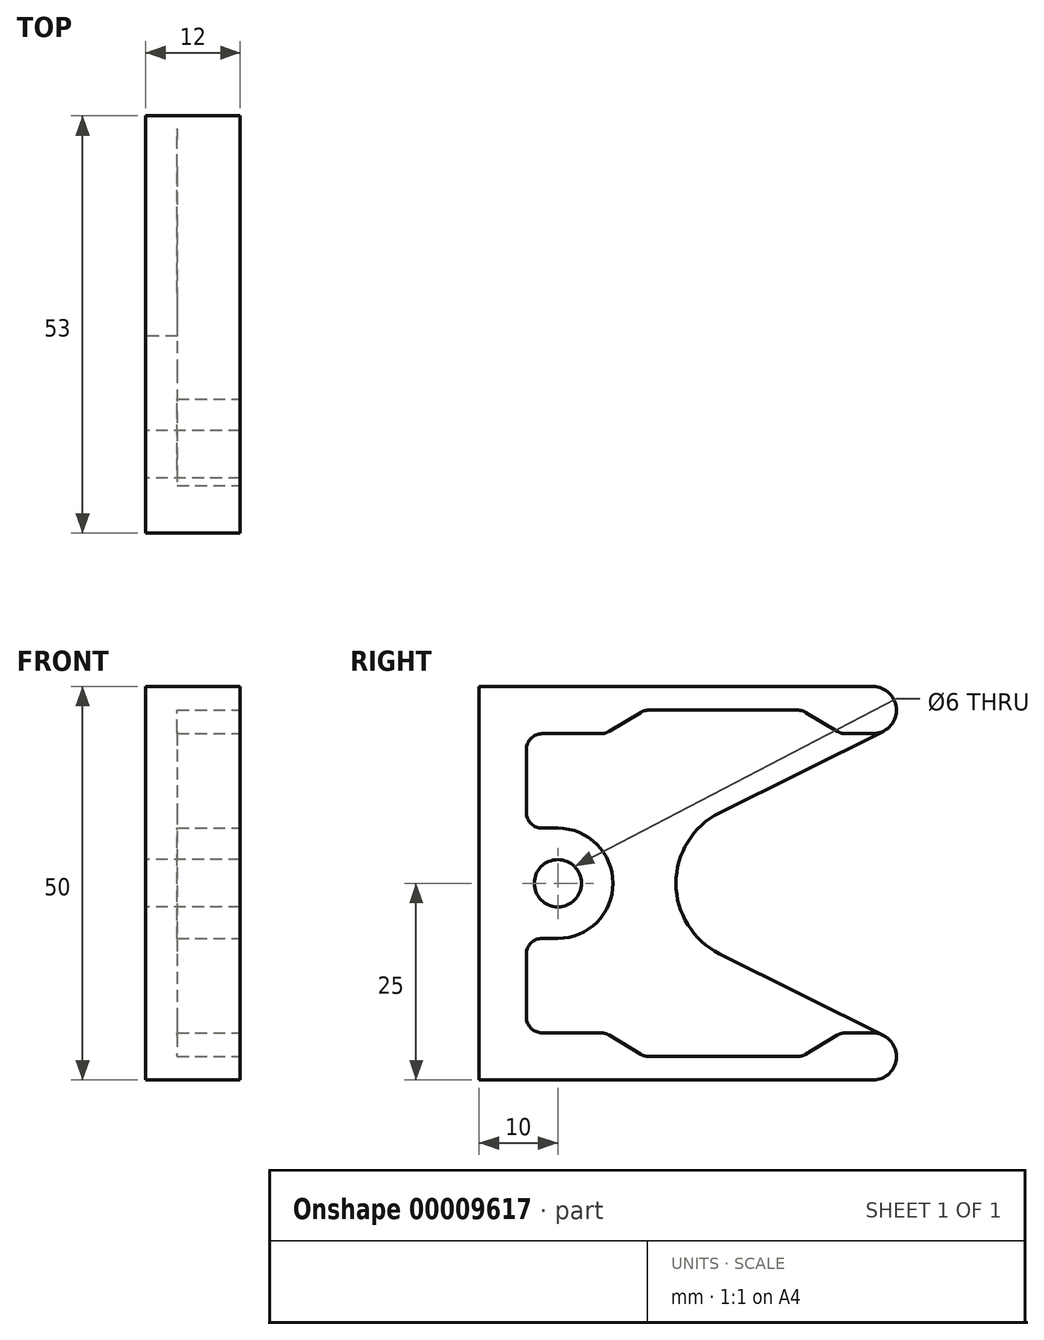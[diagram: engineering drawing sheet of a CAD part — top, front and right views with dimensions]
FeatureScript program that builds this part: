
annotation { "Feature Type Name" : "Feature", "Feature Type Description" : "" }
export const myFeature = defineFeature(function(context is Context, id is Id, definition is map)
    precondition{}
    {
        {
            var Q0;
            Q0=qCreatedBy(makeId("Right.planeOp"),FACE);
            var sketch = newSketch(context, id + "F0", { "sketchPlane" : qUnion([Q0])});
            skLineSegment(sketch, "E0", {"start": v(0, 0) * mm, "end": v(0, 50) * mm});
            skLineSegment(sketch, "E1", {"start": v(0, 50) * mm, "end": v(50, 50) * mm});
            skArc(sketch, "E2", {"start": v(51.34, 44.31) * mm, "mid": v(52.92, 47.69) * mm, "end": v(50, 50) * mm});
            skArc(sketch, "E3", {"start": v(50, 0) * mm, "mid": v(52.92, 2.31) * mm, "end": v(51.34, 5.69) * mm});
            skLineSegment(sketch, "E4", {"start": v(50, 0) * mm, "end": v(0, 0) * mm});
            skArc(sketch, "E5", {"start": v(30.54, 33.95) * mm, "mid": v(25, 25) * mm, "end": v(30.54, 16.05) * mm});
            skLineSegment(sketch, "E6", {"start": v(51.34, 44.31) * mm, "end": v(30.54, 33.95) * mm});
            skLineSegment(sketch, "E7", {"start": v(30.54, 16.05) * mm, "end": v(51.34, 5.69) * mm});
            skCircle(sketch, "E8", {"center": v(10, 25) * mm, "radius": 3 * mm});
            skSolve(sketch);
        }
        {
            var Q0;
            Q0 = qSketchRegion(id + "F0", true);
            extrude(context, id + "F1", {"entities" : qUnion([Q0]), "depth" : 12 * mm});
        }
        {
            var Q0;
            Q0=makeQuery(id+"F1.opExtrude","CAP_FACE",FACE,{"disambiguationData":[OSD([sQuery(id+"F0.wireOp",EDGE,"E0"),sQuery(id+"F0.wireOp",EDGE,"E1"),sQuery(id+"F0.wireOp",EDGE,"E2"),sQuery(id+"F0.wireOp",EDGE,"E3"),sQuery(id+"F0.wireOp",EDGE,"E4"),sQuery(id+"F0.wireOp",EDGE,"E5"),sQuery(id+"F0.wireOp",EDGE,"E6"),sQuery(id+"F0.wireOp",EDGE,"E7"),sQuery(id+"F0.wireOp",EDGE,"E8")])],"isStart":false});
            var sketch = newSketch(context, id + "F2", { "sketchPlane" : qUnion([Q0])});
            skLineSegment(sketch, "E9", {"start": v(6, 44) * mm, "end": v(6, 32) * mm});
            skLineSegment(sketch, "E10", {"start": v(6, 32) * mm, "end": v(10, 32) * mm});
            skArc(sketch, "E11", {"start": v(10, 18) * mm, "mid": v(17, 25) * mm, "end": v(10, 32) * mm});
            skLineSegment(sketch, "E12", {"start": v(10, 18) * mm, "end": v(6, 18) * mm});
            skLineSegment(sketch, "E13", {"start": v(6, 18) * mm, "end": v(6, 6) * mm});
            skLineSegment(sketch, "E14", {"start": v(6, 6) * mm, "end": v(16, 6) * mm});
            skLineSegment(sketch, "E15", {"start": v(16, 6) * mm, "end": v(21, 3) * mm});
            skLineSegment(sketch, "E16", {"start": v(21, 3) * mm, "end": v(41, 3) * mm});
            skLineSegment(sketch, "E17", {"start": v(41, 3) * mm, "end": v(46, 6) * mm});
            skLineSegment(sketch, "E18", {"start": v(46, 6) * mm, "end": v(50, 6) * mm});
            skArc(sketch, "E19", {"start": v(51.34, 5.69) * mm, "mid": v(50.69, 5.92) * mm, "end": v(50, 6) * mm});
            skArc(sketch, "E20", {"start": v(50, 44) * mm, "mid": v(50.69, 44.08) * mm, "end": v(51.34, 44.31) * mm});
            skLineSegment(sketch, "E21", {"start": v(46, 44) * mm, "end": v(41, 47) * mm});
            skLineSegment(sketch, "E22", {"start": v(41, 47) * mm, "end": v(21, 47) * mm});
            skLineSegment(sketch, "E23", {"start": v(21, 47) * mm, "end": v(16, 44) * mm});
            skLineSegment(sketch, "E24", {"start": v(16, 44) * mm, "end": v(6, 44) * mm});
            skLineSegment(sketch, "E25", {"start": v(46, 44) * mm, "end": v(50, 44) * mm});
            skSolve(sketch);
        }
        {
            var Q0;
            Q0=makeQuery(id+"F2.imprint","IMPRINT",FACE,{"disambiguationData":[TD([[makeQuery(id+"F2.imprint","IMPRINT",EDGE,{"derivedFrom":sQuery(id+"F2.wireOp",EDGE,"E9")}),1.0]])]});
            extrude(context, id + "F3", {"entities" : qUnion([Q0]), "operationType" : NewBodyOperationType.REMOVE, "oppositeDirection" : true, "depth" : 8 * mm});
        }
        {
            var Q0;
            Q0=makeQuery(id+"F3.boolean.opBoolean","COPY",EDGE,{"derivedFrom":makeQuery(id+"F3.opExtrude","SWEPT_EDGE",EDGE,{"disambiguationData":[OSD([sQuery(id+"F2.wireOp",EDGE,"E9"),sQuery(id+"F2.wireOp",EDGE,"E10")])]})});
            var Q1;
            Q1=makeQuery(id+"F3.boolean.opBoolean","COPY",EDGE,{"derivedFrom":makeQuery(id+"F3.opExtrude","SWEPT_EDGE",EDGE,{"disambiguationData":[OSD([sQuery(id+"F2.wireOp",EDGE,"E9"),sQuery(id+"F2.wireOp",EDGE,"E24")])]})});
            var Q2;
            Q2=makeQuery(id+"F3.boolean.opBoolean","COPY",EDGE,{"derivedFrom":makeQuery(id+"F3.opExtrude","SWEPT_EDGE",EDGE,{"disambiguationData":[OSD([sQuery(id+"F2.wireOp",EDGE,"E23"),sQuery(id+"F2.wireOp",EDGE,"E24")])]})});
            var Q3;
            Q3=makeQuery(id+"F3.boolean.opBoolean","COPY",EDGE,{"derivedFrom":makeQuery(id+"F3.opExtrude","SWEPT_EDGE",EDGE,{"disambiguationData":[OSD([sQuery(id+"F2.wireOp",EDGE,"E22"),sQuery(id+"F2.wireOp",EDGE,"E23")])]})});
            var Q4;
            Q4=makeQuery(id+"F3.boolean.opBoolean","COPY",EDGE,{"derivedFrom":makeQuery(id+"F3.opExtrude","SWEPT_EDGE",EDGE,{"disambiguationData":[OSD([sQuery(id+"F2.wireOp",EDGE,"E21"),sQuery(id+"F2.wireOp",EDGE,"E22")])]})});
            var Q5;
            Q5=makeQuery(id+"F3.boolean.opBoolean","COPY",EDGE,{"derivedFrom":makeQuery(id+"F3.opExtrude","SWEPT_EDGE",EDGE,{"disambiguationData":[OSD([sQuery(id+"F2.wireOp",EDGE,"E21"),sQuery(id+"F2.wireOp",EDGE,"E25")])]})});
            var Q6;
            Q6=makeQuery(id+"F3.boolean.opBoolean","COPY",EDGE,{"derivedFrom":makeQuery(id+"F3.opExtrude","SWEPT_EDGE",EDGE,{"disambiguationData":[OSD([sQuery(id+"F2.wireOp",EDGE,"E13"),sQuery(id+"F2.wireOp",EDGE,"E14")])]})});
            var Q7;
            Q7=makeQuery(id+"F3.boolean.opBoolean","COPY",EDGE,{"derivedFrom":makeQuery(id+"F3.opExtrude","SWEPT_EDGE",EDGE,{"disambiguationData":[OSD([sQuery(id+"F2.wireOp",EDGE,"E12"),sQuery(id+"F2.wireOp",EDGE,"E13")])]})});
            var Q8;
            Q8=makeQuery(id+"F3.boolean.opBoolean","COPY",EDGE,{"derivedFrom":makeQuery(id+"F3.opExtrude","SWEPT_EDGE",EDGE,{"disambiguationData":[OSD([sQuery(id+"F2.wireOp",EDGE,"E14"),sQuery(id+"F2.wireOp",EDGE,"E15")])]})});
            var Q9;
            Q9=makeQuery(id+"F3.boolean.opBoolean","COPY",EDGE,{"derivedFrom":makeQuery(id+"F3.opExtrude","SWEPT_EDGE",EDGE,{"disambiguationData":[OSD([sQuery(id+"F2.wireOp",EDGE,"E15"),sQuery(id+"F2.wireOp",EDGE,"E16")])]})});
            var Q10;
            Q10=makeQuery(id+"F3.boolean.opBoolean","COPY",EDGE,{"derivedFrom":makeQuery(id+"F3.opExtrude","SWEPT_EDGE",EDGE,{"disambiguationData":[OSD([sQuery(id+"F2.wireOp",EDGE,"E16"),sQuery(id+"F2.wireOp",EDGE,"E17")])]})});
            var Q11;
            Q11=makeQuery(id+"F3.boolean.opBoolean","COPY",EDGE,{"derivedFrom":makeQuery(id+"F3.opExtrude","SWEPT_EDGE",EDGE,{"disambiguationData":[OSD([sQuery(id+"F2.wireOp",EDGE,"E17"),sQuery(id+"F2.wireOp",EDGE,"E18")])]})});
            fillet(context, id + "F4", {"entities" : qUnion([Q0, Q1, Q2, Q3, Q4, Q5, Q6, Q7, Q8, Q9, Q10, Q11]), "radius" : 2 * mm, "tangentPropagation" : true, "allowEdgeOverflow" : false});
        }
    });
